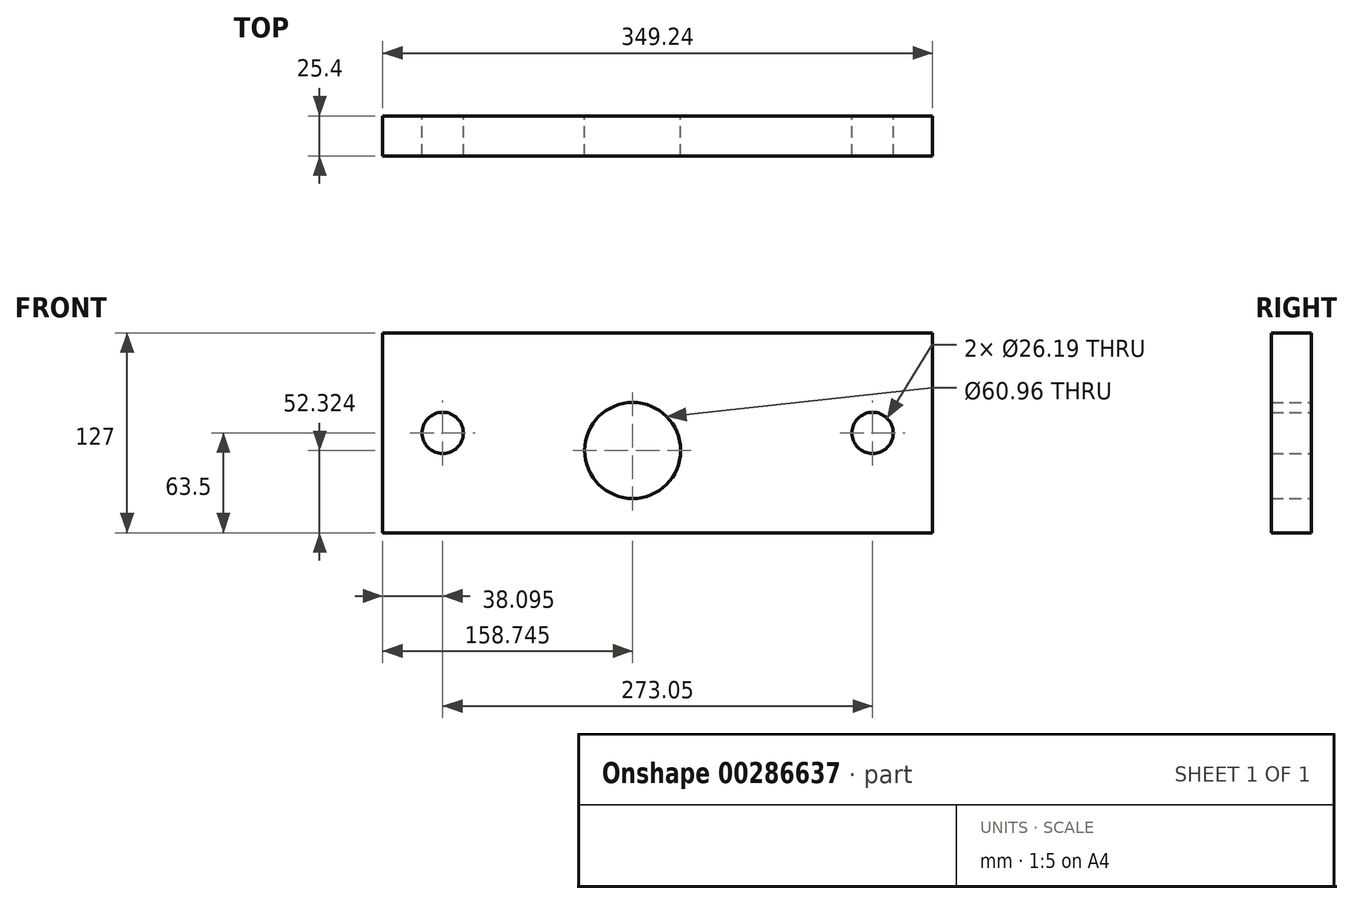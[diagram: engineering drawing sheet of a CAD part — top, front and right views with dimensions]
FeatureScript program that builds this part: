
annotation { "Feature Type Name" : "Feature", "Feature Type Description" : "" }
export const myFeature = defineFeature(function(context is Context, id is Id, definition is map)
    precondition{}
    {
        {
            var Q0;
            Q0=qCreatedBy(makeId("Front.planeOp"),FACE);
            var sketch = newSketch(context, id + "F0", { "sketchPlane" : qUnion([Q0])});
            skLineSegment(sketch, "E0.bottom", {"start": v(174.62, 63.5) * mm, "end": v(-174.63, 63.5) * mm});
            skLineSegment(sketch, "E0.top", {"start": v(174.63, -63.5) * mm, "end": v(-174.62, -63.5) * mm});
            skLineSegment(sketch, "E0.left", {"start": v(174.62, 63.5) * mm, "end": v(174.63, -63.5) * mm});
            skLineSegment(sketch, "E0.right", {"start": v(-174.63, 63.5) * mm, "end": v(-174.62, -63.5) * mm});
            skPoint(sketch, "E0.middle", {"position": v(0, 0) * mm});
            skCircle(sketch, "E1", {"center": v(-136.53, 0) * mm, "radius": 13.1 * mm});
            skCircle(sketch, "E2", {"center": v(136.53, 0) * mm, "radius": 13.1 * mm});
            skCircle(sketch, "E3", {"center": v(-15.88, -11.18) * mm, "radius": 30.48 * mm});
            skSolve(sketch);
        }
        {
            var Q0;
            Q0 = qSketchRegion(id + "F0", true);
            extrude(context, id + "F1", {"entities" : qUnion([Q0]), "depth" : 25.4 * mm});
        }
    });
